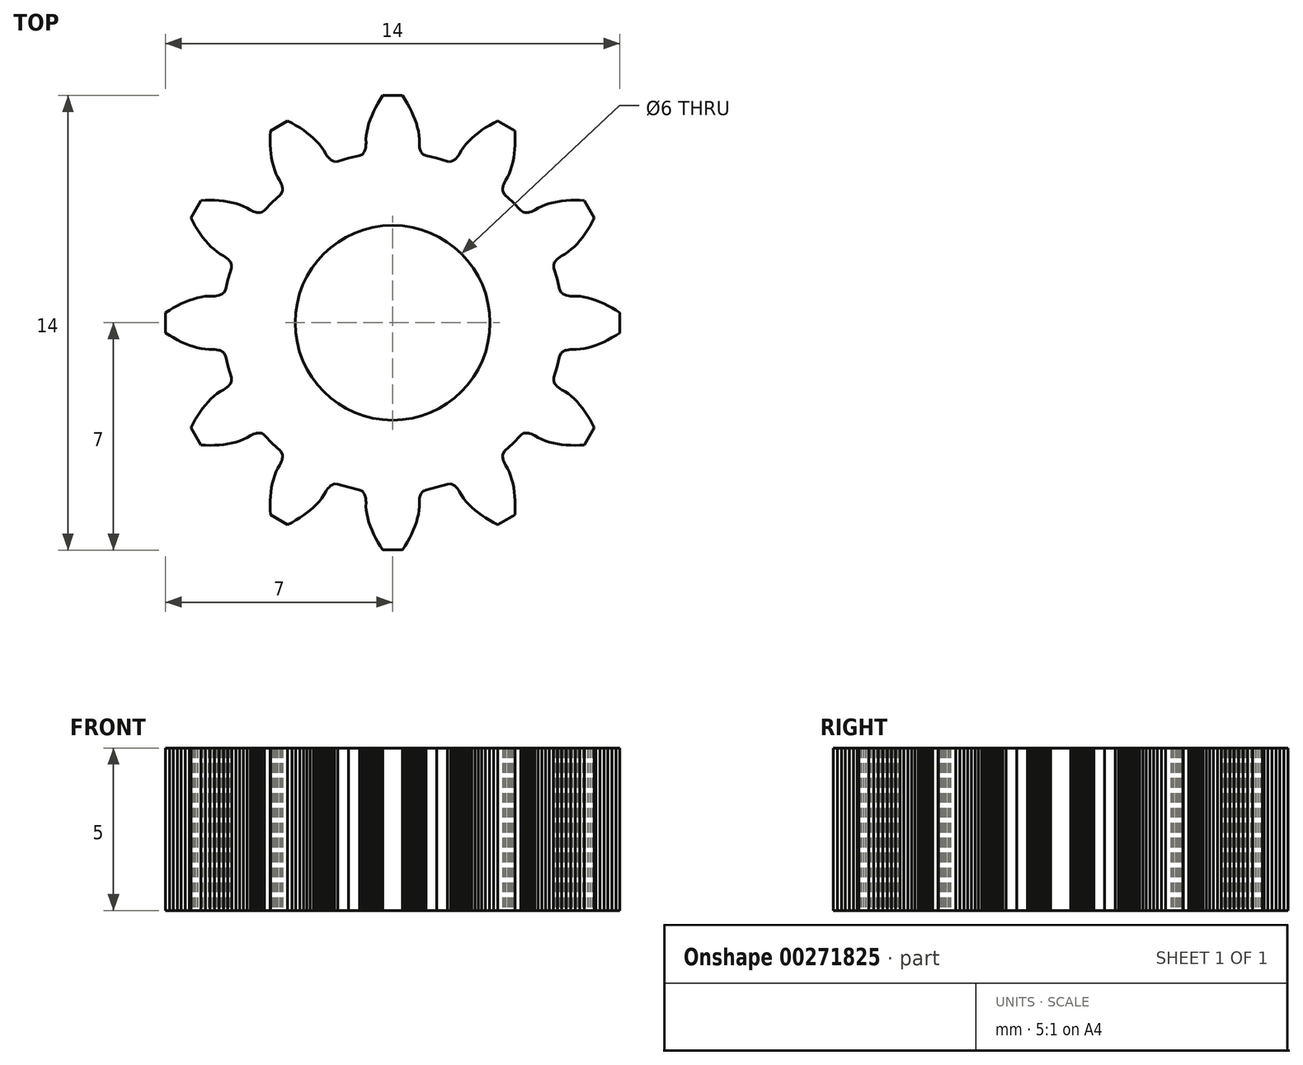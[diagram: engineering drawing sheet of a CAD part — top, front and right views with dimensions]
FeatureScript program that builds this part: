
annotation { "Feature Type Name" : "Feature", "Feature Type Description" : "" }
export const myFeature = defineFeature(function(context is Context, id is Id, definition is map)
    precondition{}
    {
        {
            var Q0;
            Q0=qCreatedBy(makeId("Top.planeOp"),FACE);
            var sketch = newSketch(context, id + "F0", { "sketchPlane" : qUnion([Q0])});
            skLineSegment(sketch, "E0", {"start": v(5.15, 1.02) * mm, "end": v(5.2, 0.93) * mm});
            skLineSegment(sketch, "E1", {"start": v(5.2, 0.93) * mm, "end": v(5.23, 0.9) * mm});
            skLineSegment(sketch, "E2", {"start": v(5.23, 0.9) * mm, "end": v(5.26, 0.88) * mm});
            skLineSegment(sketch, "E3", {"start": v(5.26, 0.88) * mm, "end": v(5.3, 0.86) * mm});
            skLineSegment(sketch, "E4", {"start": v(5.3, 0.86) * mm, "end": v(5.33, 0.85) * mm});
            skLineSegment(sketch, "E5", {"start": v(5.33, 0.85) * mm, "end": v(5.36, 0.84) * mm});
            skLineSegment(sketch, "E6", {"start": v(5.36, 0.84) * mm, "end": v(5.42, 0.83) * mm});
            skLineSegment(sketch, "E7", {"start": v(5.42, 0.83) * mm, "end": v(5.48, 0.82) * mm});
            skLineSegment(sketch, "E8", {"start": v(5.48, 0.82) * mm, "end": v(5.54, 0.82) * mm});
            skLineSegment(sketch, "E9", {"start": v(5.54, 0.82) * mm, "end": v(5.66, 0.82) * mm});
            skLineSegment(sketch, "E10", {"start": v(5.66, 0.82) * mm, "end": v(5.78, 0.81) * mm});
            skLineSegment(sketch, "E11", {"start": v(5.78, 0.81) * mm, "end": v(5.9, 0.8) * mm});
            skLineSegment(sketch, "E12", {"start": v(5.9, 0.8) * mm, "end": v(6.02, 0.77) * mm});
            skLineSegment(sketch, "E13", {"start": v(6.02, 0.77) * mm, "end": v(6.14, 0.73) * mm});
            skLineSegment(sketch, "E14", {"start": v(6.14, 0.73) * mm, "end": v(6.26, 0.69) * mm});
            skLineSegment(sketch, "E15", {"start": v(6.26, 0.69) * mm, "end": v(6.39, 0.64) * mm});
            skLineSegment(sketch, "E16", {"start": v(6.39, 0.64) * mm, "end": v(6.5, 0.59) * mm});
            skLineSegment(sketch, "E17", {"start": v(6.5, 0.59) * mm, "end": v(6.63, 0.52) * mm});
            skLineSegment(sketch, "E18", {"start": v(6.63, 0.52) * mm, "end": v(6.75, 0.46) * mm});
            skLineSegment(sketch, "E19", {"start": v(6.75, 0.46) * mm, "end": v(6.88, 0.39) * mm});
            skLineSegment(sketch, "E20", {"start": v(6.88, 0.39) * mm, "end": v(7, 0.3) * mm});
            skLineSegment(sketch, "E21", {"start": v(7, 0.3) * mm, "end": v(7, -0.3) * mm});
            skLineSegment(sketch, "E22", {"start": v(7, -0.3) * mm, "end": v(6.88, -0.39) * mm});
            skLineSegment(sketch, "E23", {"start": v(6.88, -0.39) * mm, "end": v(6.75, -0.46) * mm});
            skLineSegment(sketch, "E24", {"start": v(6.75, -0.46) * mm, "end": v(6.63, -0.52) * mm});
            skLineSegment(sketch, "E25", {"start": v(6.63, -0.52) * mm, "end": v(6.5, -0.59) * mm});
            skLineSegment(sketch, "E26", {"start": v(6.5, -0.59) * mm, "end": v(6.39, -0.64) * mm});
            skLineSegment(sketch, "E27", {"start": v(6.39, -0.64) * mm, "end": v(6.26, -0.69) * mm});
            skLineSegment(sketch, "E28", {"start": v(6.26, -0.69) * mm, "end": v(6.14, -0.73) * mm});
            skLineSegment(sketch, "E29", {"start": v(6.14, -0.73) * mm, "end": v(6.02, -0.77) * mm});
            skLineSegment(sketch, "E30", {"start": v(6.02, -0.77) * mm, "end": v(5.9, -0.8) * mm});
            skLineSegment(sketch, "E31", {"start": v(5.9, -0.8) * mm, "end": v(5.78, -0.81) * mm});
            skLineSegment(sketch, "E32", {"start": v(5.78, -0.81) * mm, "end": v(5.66, -0.82) * mm});
            skLineSegment(sketch, "E33", {"start": v(5.66, -0.82) * mm, "end": v(5.54, -0.82) * mm});
            skLineSegment(sketch, "E34", {"start": v(5.54, -0.82) * mm, "end": v(5.48, -0.82) * mm});
            skLineSegment(sketch, "E35", {"start": v(5.48, -0.82) * mm, "end": v(5.42, -0.83) * mm});
            skLineSegment(sketch, "E36", {"start": v(5.42, -0.83) * mm, "end": v(5.36, -0.84) * mm});
            skLineSegment(sketch, "E37", {"start": v(5.36, -0.84) * mm, "end": v(5.33, -0.85) * mm});
            skLineSegment(sketch, "E38", {"start": v(5.33, -0.85) * mm, "end": v(5.3, -0.86) * mm});
            skLineSegment(sketch, "E39", {"start": v(5.3, -0.86) * mm, "end": v(5.26, -0.88) * mm});
            skLineSegment(sketch, "E40", {"start": v(5.26, -0.88) * mm, "end": v(5.23, -0.9) * mm});
            skLineSegment(sketch, "E41", {"start": v(5.23, -0.9) * mm, "end": v(5.2, -0.93) * mm});
            skLineSegment(sketch, "E42", {"start": v(5.2, -0.93) * mm, "end": v(5.15, -1.02) * mm});
            skLineSegment(sketch, "E43", {"start": v(5.15, -1.02) * mm, "end": v(5.07, -1.36) * mm});
            skLineSegment(sketch, "E44", {"start": v(5.07, -1.36) * mm, "end": v(4.97, -1.69) * mm});
            skLineSegment(sketch, "E45", {"start": v(4.97, -1.69) * mm, "end": v(4.96, -1.79) * mm});
            skLineSegment(sketch, "E46", {"start": v(4.96, -1.79) * mm, "end": v(4.98, -1.83) * mm});
            skLineSegment(sketch, "E47", {"start": v(4.98, -1.83) * mm, "end": v(5, -1.87) * mm});
            skLineSegment(sketch, "E48", {"start": v(5, -1.87) * mm, "end": v(5.02, -1.9) * mm});
            skLineSegment(sketch, "E49", {"start": v(5.02, -1.9) * mm, "end": v(5.04, -1.93) * mm});
            skLineSegment(sketch, "E50", {"start": v(5.04, -1.93) * mm, "end": v(5.06, -1.95) * mm});
            skLineSegment(sketch, "E51", {"start": v(5.06, -1.95) * mm, "end": v(5.1, -2) * mm});
            skLineSegment(sketch, "E52", {"start": v(5.1, -2) * mm, "end": v(5.15, -2.03) * mm});
            skLineSegment(sketch, "E53", {"start": v(5.15, -2.03) * mm, "end": v(5.2, -2.06) * mm});
            skLineSegment(sketch, "E54", {"start": v(5.2, -2.06) * mm, "end": v(5.3, -2.12) * mm});
            skLineSegment(sketch, "E55", {"start": v(5.3, -2.12) * mm, "end": v(5.4, -2.18) * mm});
            skLineSegment(sketch, "E56", {"start": v(5.4, -2.18) * mm, "end": v(5.5, -2.26) * mm});
            skLineSegment(sketch, "E57", {"start": v(5.5, -2.26) * mm, "end": v(5.6, -2.35) * mm});
            skLineSegment(sketch, "E58", {"start": v(5.6, -2.35) * mm, "end": v(5.68, -2.44) * mm});
            skLineSegment(sketch, "E59", {"start": v(5.68, -2.44) * mm, "end": v(5.77, -2.53) * mm});
            skLineSegment(sketch, "E60", {"start": v(5.77, -2.53) * mm, "end": v(5.85, -2.64) * mm});
            skLineSegment(sketch, "E61", {"start": v(5.85, -2.64) * mm, "end": v(5.93, -2.75) * mm});
            skLineSegment(sketch, "E62", {"start": v(5.93, -2.75) * mm, "end": v(6, -2.86) * mm});
            skLineSegment(sketch, "E63", {"start": v(6, -2.86) * mm, "end": v(6.08, -2.98) * mm});
            skLineSegment(sketch, "E64", {"start": v(6.08, -2.98) * mm, "end": v(6.15, -3.1) * mm});
            skLineSegment(sketch, "E65", {"start": v(6.15, -3.1) * mm, "end": v(6.21, -3.23) * mm});
            skLineSegment(sketch, "E66", {"start": v(6.21, -3.23) * mm, "end": v(5.9, -3.76) * mm});
            skLineSegment(sketch, "E67", {"start": v(5.9, -3.76) * mm, "end": v(5.76, -3.77) * mm});
            skLineSegment(sketch, "E68", {"start": v(5.76, -3.77) * mm, "end": v(5.62, -3.77) * mm});
            skLineSegment(sketch, "E69", {"start": v(5.62, -3.77) * mm, "end": v(5.48, -3.77) * mm});
            skLineSegment(sketch, "E70", {"start": v(5.48, -3.77) * mm, "end": v(5.34, -3.76) * mm});
            skLineSegment(sketch, "E71", {"start": v(5.34, -3.76) * mm, "end": v(5.21, -3.75) * mm});
            skLineSegment(sketch, "E72", {"start": v(5.21, -3.75) * mm, "end": v(5.08, -3.73) * mm});
            skLineSegment(sketch, "E73", {"start": v(5.08, -3.73) * mm, "end": v(4.95, -3.7) * mm});
            skLineSegment(sketch, "E74", {"start": v(4.95, -3.7) * mm, "end": v(4.83, -3.67) * mm});
            skLineSegment(sketch, "E75", {"start": v(4.83, -3.67) * mm, "end": v(4.7, -3.64) * mm});
            skLineSegment(sketch, "E76", {"start": v(4.7, -3.64) * mm, "end": v(4.6, -3.6) * mm});
            skLineSegment(sketch, "E77", {"start": v(4.6, -3.6) * mm, "end": v(4.49, -3.54) * mm});
            skLineSegment(sketch, "E78", {"start": v(4.49, -3.54) * mm, "end": v(4.39, -3.48) * mm});
            skLineSegment(sketch, "E79", {"start": v(4.39, -3.48) * mm, "end": v(4.33, -3.45) * mm});
            skLineSegment(sketch, "E80", {"start": v(4.33, -3.45) * mm, "end": v(4.28, -3.43) * mm});
            skLineSegment(sketch, "E81", {"start": v(4.28, -3.43) * mm, "end": v(4.22, -3.4) * mm});
            skLineSegment(sketch, "E82", {"start": v(4.22, -3.4) * mm, "end": v(4.19, -3.4) * mm});
            skLineSegment(sketch, "E83", {"start": v(4.19, -3.4) * mm, "end": v(4.15, -3.4) * mm});
            skLineSegment(sketch, "E84", {"start": v(4.15, -3.4) * mm, "end": v(4.12, -3.4) * mm});
            skLineSegment(sketch, "E85", {"start": v(4.12, -3.4) * mm, "end": v(4.08, -3.4) * mm});
            skLineSegment(sketch, "E86", {"start": v(4.08, -3.4) * mm, "end": v(4.03, -3.4) * mm});
            skLineSegment(sketch, "E87", {"start": v(4.03, -3.4) * mm, "end": v(3.94, -3.46) * mm});
            skLineSegment(sketch, "E88", {"start": v(3.94, -3.46) * mm, "end": v(3.7, -3.7) * mm});
            skLineSegment(sketch, "E89", {"start": v(3.7, -3.7) * mm, "end": v(3.46, -3.94) * mm});
            skLineSegment(sketch, "E90", {"start": v(3.46, -3.94) * mm, "end": v(3.4, -4.03) * mm});
            skLineSegment(sketch, "E91", {"start": v(3.4, -4.03) * mm, "end": v(3.4, -4.08) * mm});
            skLineSegment(sketch, "E92", {"start": v(3.4, -4.08) * mm, "end": v(3.4, -4.12) * mm});
            skLineSegment(sketch, "E93", {"start": v(3.4, -4.12) * mm, "end": v(3.4, -4.15) * mm});
            skLineSegment(sketch, "E94", {"start": v(3.4, -4.15) * mm, "end": v(3.4, -4.19) * mm});
            skLineSegment(sketch, "E95", {"start": v(3.4, -4.19) * mm, "end": v(3.4, -4.22) * mm});
            skLineSegment(sketch, "E96", {"start": v(3.4, -4.22) * mm, "end": v(3.43, -4.28) * mm});
            skLineSegment(sketch, "E97", {"start": v(3.43, -4.28) * mm, "end": v(3.45, -4.33) * mm});
            skLineSegment(sketch, "E98", {"start": v(3.45, -4.33) * mm, "end": v(3.48, -4.39) * mm});
            skLineSegment(sketch, "E99", {"start": v(3.48, -4.39) * mm, "end": v(3.54, -4.49) * mm});
            skLineSegment(sketch, "E100", {"start": v(3.54, -4.49) * mm, "end": v(3.6, -4.6) * mm});
            skLineSegment(sketch, "E101", {"start": v(3.6, -4.6) * mm, "end": v(3.64, -4.7) * mm});
            skLineSegment(sketch, "E102", {"start": v(3.64, -4.7) * mm, "end": v(3.67, -4.83) * mm});
            skLineSegment(sketch, "E103", {"start": v(3.67, -4.83) * mm, "end": v(3.7, -4.95) * mm});
            skLineSegment(sketch, "E104", {"start": v(3.7, -4.95) * mm, "end": v(3.73, -5.08) * mm});
            skLineSegment(sketch, "E105", {"start": v(3.73, -5.08) * mm, "end": v(3.75, -5.21) * mm});
            skLineSegment(sketch, "E106", {"start": v(3.75, -5.21) * mm, "end": v(3.76, -5.34) * mm});
            skLineSegment(sketch, "E107", {"start": v(3.76, -5.34) * mm, "end": v(3.77, -5.48) * mm});
            skLineSegment(sketch, "E108", {"start": v(3.77, -5.48) * mm, "end": v(3.77, -5.62) * mm});
            skLineSegment(sketch, "E109", {"start": v(3.77, -5.62) * mm, "end": v(3.77, -5.76) * mm});
            skLineSegment(sketch, "E110", {"start": v(3.77, -5.76) * mm, "end": v(3.76, -5.9) * mm});
            skLineSegment(sketch, "E111", {"start": v(3.76, -5.9) * mm, "end": v(3.23, -6.21) * mm});
            skLineSegment(sketch, "E112", {"start": v(3.23, -6.21) * mm, "end": v(3.1, -6.15) * mm});
            skLineSegment(sketch, "E113", {"start": v(3.1, -6.15) * mm, "end": v(2.98, -6.08) * mm});
            skLineSegment(sketch, "E114", {"start": v(2.98, -6.08) * mm, "end": v(2.86, -6) * mm});
            skLineSegment(sketch, "E115", {"start": v(2.86, -6) * mm, "end": v(2.75, -5.93) * mm});
            skLineSegment(sketch, "E116", {"start": v(2.75, -5.93) * mm, "end": v(2.64, -5.85) * mm});
            skLineSegment(sketch, "E117", {"start": v(2.64, -5.85) * mm, "end": v(2.53, -5.77) * mm});
            skLineSegment(sketch, "E118", {"start": v(2.53, -5.77) * mm, "end": v(2.44, -5.68) * mm});
            skLineSegment(sketch, "E119", {"start": v(2.44, -5.68) * mm, "end": v(2.35, -5.6) * mm});
            skLineSegment(sketch, "E120", {"start": v(2.35, -5.6) * mm, "end": v(2.26, -5.5) * mm});
            skLineSegment(sketch, "E121", {"start": v(2.26, -5.5) * mm, "end": v(2.18, -5.4) * mm});
            skLineSegment(sketch, "E122", {"start": v(2.18, -5.4) * mm, "end": v(2.12, -5.3) * mm});
            skLineSegment(sketch, "E123", {"start": v(2.12, -5.3) * mm, "end": v(2.06, -5.2) * mm});
            skLineSegment(sketch, "E124", {"start": v(2.06, -5.2) * mm, "end": v(2.03, -5.15) * mm});
            skLineSegment(sketch, "E125", {"start": v(2.03, -5.15) * mm, "end": v(2, -5.1) * mm});
            skLineSegment(sketch, "E126", {"start": v(2, -5.1) * mm, "end": v(1.95, -5.06) * mm});
            skLineSegment(sketch, "E127", {"start": v(1.95, -5.06) * mm, "end": v(1.93, -5.04) * mm});
            skLineSegment(sketch, "E128", {"start": v(1.93, -5.04) * mm, "end": v(1.9, -5.02) * mm});
            skLineSegment(sketch, "E129", {"start": v(1.9, -5.02) * mm, "end": v(1.87, -5) * mm});
            skLineSegment(sketch, "E130", {"start": v(1.87, -5) * mm, "end": v(1.83, -4.98) * mm});
            skLineSegment(sketch, "E131", {"start": v(1.83, -4.98) * mm, "end": v(1.79, -4.96) * mm});
            skLineSegment(sketch, "E132", {"start": v(1.79, -4.96) * mm, "end": v(1.69, -4.97) * mm});
            skLineSegment(sketch, "E133", {"start": v(1.69, -4.97) * mm, "end": v(1.36, -5.07) * mm});
            skLineSegment(sketch, "E134", {"start": v(1.36, -5.07) * mm, "end": v(1.02, -5.15) * mm});
            skLineSegment(sketch, "E135", {"start": v(1.02, -5.15) * mm, "end": v(0.93, -5.2) * mm});
            skLineSegment(sketch, "E136", {"start": v(0.93, -5.2) * mm, "end": v(0.9, -5.23) * mm});
            skLineSegment(sketch, "E137", {"start": v(0.9, -5.23) * mm, "end": v(0.88, -5.26) * mm});
            skLineSegment(sketch, "E138", {"start": v(0.88, -5.26) * mm, "end": v(0.86, -5.3) * mm});
            skLineSegment(sketch, "E139", {"start": v(0.86, -5.3) * mm, "end": v(0.85, -5.33) * mm});
            skLineSegment(sketch, "E140", {"start": v(0.85, -5.33) * mm, "end": v(0.84, -5.36) * mm});
            skLineSegment(sketch, "E141", {"start": v(0.84, -5.36) * mm, "end": v(0.83, -5.42) * mm});
            skLineSegment(sketch, "E142", {"start": v(0.83, -5.42) * mm, "end": v(0.82, -5.48) * mm});
            skLineSegment(sketch, "E143", {"start": v(0.82, -5.48) * mm, "end": v(0.82, -5.54) * mm});
            skLineSegment(sketch, "E144", {"start": v(0.82, -5.54) * mm, "end": v(0.82, -5.66) * mm});
            skLineSegment(sketch, "E145", {"start": v(0.82, -5.66) * mm, "end": v(0.81, -5.78) * mm});
            skLineSegment(sketch, "E146", {"start": v(0.81, -5.78) * mm, "end": v(0.8, -5.9) * mm});
            skLineSegment(sketch, "E147", {"start": v(0.8, -5.9) * mm, "end": v(0.77, -6.02) * mm});
            skLineSegment(sketch, "E148", {"start": v(0.77, -6.02) * mm, "end": v(0.73, -6.14) * mm});
            skLineSegment(sketch, "E149", {"start": v(0.73, -6.14) * mm, "end": v(0.69, -6.26) * mm});
            skLineSegment(sketch, "E150", {"start": v(0.69, -6.26) * mm, "end": v(0.64, -6.39) * mm});
            skLineSegment(sketch, "E151", {"start": v(0.64, -6.39) * mm, "end": v(0.59, -6.5) * mm});
            skLineSegment(sketch, "E152", {"start": v(0.59, -6.5) * mm, "end": v(0.52, -6.63) * mm});
            skLineSegment(sketch, "E153", {"start": v(0.52, -6.63) * mm, "end": v(0.46, -6.75) * mm});
            skLineSegment(sketch, "E154", {"start": v(0.46, -6.75) * mm, "end": v(0.39, -6.88) * mm});
            skLineSegment(sketch, "E155", {"start": v(0.39, -6.88) * mm, "end": v(0.3, -7) * mm});
            skLineSegment(sketch, "E156", {"start": v(0.3, -7) * mm, "end": v(-0.3, -7) * mm});
            skLineSegment(sketch, "E157", {"start": v(-0.3, -7) * mm, "end": v(-0.39, -6.88) * mm});
            skLineSegment(sketch, "E158", {"start": v(-0.39, -6.88) * mm, "end": v(-0.46, -6.75) * mm});
            skLineSegment(sketch, "E159", {"start": v(-0.46, -6.75) * mm, "end": v(-0.52, -6.63) * mm});
            skLineSegment(sketch, "E160", {"start": v(-0.52, -6.63) * mm, "end": v(-0.59, -6.5) * mm});
            skLineSegment(sketch, "E161", {"start": v(-0.59, -6.5) * mm, "end": v(-0.64, -6.39) * mm});
            skLineSegment(sketch, "E162", {"start": v(-0.64, -6.39) * mm, "end": v(-0.69, -6.26) * mm});
            skLineSegment(sketch, "E163", {"start": v(-0.69, -6.26) * mm, "end": v(-0.73, -6.14) * mm});
            skLineSegment(sketch, "E164", {"start": v(-0.73, -6.14) * mm, "end": v(-0.77, -6.02) * mm});
            skLineSegment(sketch, "E165", {"start": v(-0.77, -6.02) * mm, "end": v(-0.8, -5.9) * mm});
            skLineSegment(sketch, "E166", {"start": v(-0.8, -5.9) * mm, "end": v(-0.81, -5.78) * mm});
            skLineSegment(sketch, "E167", {"start": v(-0.81, -5.78) * mm, "end": v(-0.82, -5.66) * mm});
            skLineSegment(sketch, "E168", {"start": v(-0.82, -5.66) * mm, "end": v(-0.82, -5.54) * mm});
            skLineSegment(sketch, "E169", {"start": v(-0.82, -5.54) * mm, "end": v(-0.82, -5.48) * mm});
            skLineSegment(sketch, "E170", {"start": v(-0.82, -5.48) * mm, "end": v(-0.83, -5.42) * mm});
            skLineSegment(sketch, "E171", {"start": v(-0.83, -5.42) * mm, "end": v(-0.84, -5.36) * mm});
            skLineSegment(sketch, "E172", {"start": v(-0.84, -5.36) * mm, "end": v(-0.85, -5.33) * mm});
            skLineSegment(sketch, "E173", {"start": v(-0.85, -5.33) * mm, "end": v(-0.86, -5.3) * mm});
            skLineSegment(sketch, "E174", {"start": v(-0.86, -5.3) * mm, "end": v(-0.88, -5.26) * mm});
            skLineSegment(sketch, "E175", {"start": v(-0.88, -5.26) * mm, "end": v(-0.9, -5.23) * mm});
            skLineSegment(sketch, "E176", {"start": v(-0.9, -5.23) * mm, "end": v(-0.93, -5.2) * mm});
            skLineSegment(sketch, "E177", {"start": v(-0.93, -5.2) * mm, "end": v(-1.02, -5.15) * mm});
            skLineSegment(sketch, "E178", {"start": v(-1.02, -5.15) * mm, "end": v(-1.36, -5.07) * mm});
            skLineSegment(sketch, "E179", {"start": v(-1.36, -5.07) * mm, "end": v(-1.69, -4.97) * mm});
            skLineSegment(sketch, "E180", {"start": v(-1.69, -4.97) * mm, "end": v(-1.79, -4.96) * mm});
            skLineSegment(sketch, "E181", {"start": v(-1.79, -4.96) * mm, "end": v(-1.83, -4.98) * mm});
            skLineSegment(sketch, "E182", {"start": v(-1.83, -4.98) * mm, "end": v(-1.87, -5) * mm});
            skLineSegment(sketch, "E183", {"start": v(-1.87, -5) * mm, "end": v(-1.9, -5.02) * mm});
            skLineSegment(sketch, "E184", {"start": v(-1.9, -5.02) * mm, "end": v(-1.93, -5.04) * mm});
            skLineSegment(sketch, "E185", {"start": v(-1.93, -5.04) * mm, "end": v(-1.95, -5.06) * mm});
            skLineSegment(sketch, "E186", {"start": v(-1.95, -5.06) * mm, "end": v(-2, -5.1) * mm});
            skLineSegment(sketch, "E187", {"start": v(-2, -5.1) * mm, "end": v(-2.03, -5.15) * mm});
            skLineSegment(sketch, "E188", {"start": v(-2.03, -5.15) * mm, "end": v(-2.06, -5.2) * mm});
            skLineSegment(sketch, "E189", {"start": v(-2.06, -5.2) * mm, "end": v(-2.12, -5.3) * mm});
            skLineSegment(sketch, "E190", {"start": v(-2.12, -5.3) * mm, "end": v(-2.18, -5.4) * mm});
            skLineSegment(sketch, "E191", {"start": v(-2.18, -5.4) * mm, "end": v(-2.26, -5.5) * mm});
            skLineSegment(sketch, "E192", {"start": v(-2.26, -5.5) * mm, "end": v(-2.35, -5.6) * mm});
            skLineSegment(sketch, "E193", {"start": v(-2.35, -5.6) * mm, "end": v(-2.44, -5.68) * mm});
            skLineSegment(sketch, "E194", {"start": v(-2.44, -5.68) * mm, "end": v(-2.53, -5.77) * mm});
            skLineSegment(sketch, "E195", {"start": v(-2.53, -5.77) * mm, "end": v(-2.64, -5.85) * mm});
            skLineSegment(sketch, "E196", {"start": v(-2.64, -5.85) * mm, "end": v(-2.75, -5.93) * mm});
            skLineSegment(sketch, "E197", {"start": v(-2.75, -5.93) * mm, "end": v(-2.86, -6) * mm});
            skLineSegment(sketch, "E198", {"start": v(-2.86, -6) * mm, "end": v(-2.98, -6.08) * mm});
            skLineSegment(sketch, "E199", {"start": v(-2.98, -6.08) * mm, "end": v(-3.1, -6.15) * mm});
            skLineSegment(sketch, "E200", {"start": v(-3.1, -6.15) * mm, "end": v(-3.23, -6.21) * mm});
            skLineSegment(sketch, "E201", {"start": v(-3.23, -6.21) * mm, "end": v(-3.76, -5.9) * mm});
            skLineSegment(sketch, "E202", {"start": v(-3.76, -5.9) * mm, "end": v(-3.77, -5.76) * mm});
            skLineSegment(sketch, "E203", {"start": v(-3.77, -5.76) * mm, "end": v(-3.77, -5.62) * mm});
            skLineSegment(sketch, "E204", {"start": v(-3.77, -5.62) * mm, "end": v(-3.77, -5.48) * mm});
            skLineSegment(sketch, "E205", {"start": v(-3.77, -5.48) * mm, "end": v(-3.76, -5.34) * mm});
            skLineSegment(sketch, "E206", {"start": v(-3.76, -5.34) * mm, "end": v(-3.75, -5.21) * mm});
            skLineSegment(sketch, "E207", {"start": v(-3.75, -5.21) * mm, "end": v(-3.73, -5.08) * mm});
            skLineSegment(sketch, "E208", {"start": v(-3.73, -5.08) * mm, "end": v(-3.7, -4.95) * mm});
            skLineSegment(sketch, "E209", {"start": v(-3.7, -4.95) * mm, "end": v(-3.67, -4.83) * mm});
            skLineSegment(sketch, "E210", {"start": v(-3.67, -4.83) * mm, "end": v(-3.64, -4.7) * mm});
            skLineSegment(sketch, "E211", {"start": v(-3.64, -4.7) * mm, "end": v(-3.6, -4.6) * mm});
            skLineSegment(sketch, "E212", {"start": v(-3.6, -4.6) * mm, "end": v(-3.54, -4.49) * mm});
            skLineSegment(sketch, "E213", {"start": v(-3.54, -4.49) * mm, "end": v(-3.48, -4.39) * mm});
            skLineSegment(sketch, "E214", {"start": v(-3.48, -4.39) * mm, "end": v(-3.45, -4.33) * mm});
            skLineSegment(sketch, "E215", {"start": v(-3.45, -4.33) * mm, "end": v(-3.43, -4.28) * mm});
            skLineSegment(sketch, "E216", {"start": v(-3.43, -4.28) * mm, "end": v(-3.4, -4.22) * mm});
            skLineSegment(sketch, "E217", {"start": v(-3.4, -4.22) * mm, "end": v(-3.4, -4.19) * mm});
            skLineSegment(sketch, "E218", {"start": v(-3.4, -4.19) * mm, "end": v(-3.4, -4.15) * mm});
            skLineSegment(sketch, "E219", {"start": v(-3.4, -4.15) * mm, "end": v(-3.4, -4.12) * mm});
            skLineSegment(sketch, "E220", {"start": v(-3.4, -4.12) * mm, "end": v(-3.4, -4.08) * mm});
            skLineSegment(sketch, "E221", {"start": v(-3.4, -4.08) * mm, "end": v(-3.4, -4.03) * mm});
            skLineSegment(sketch, "E222", {"start": v(-3.4, -4.03) * mm, "end": v(-3.46, -3.94) * mm});
            skLineSegment(sketch, "E223", {"start": v(-3.46, -3.94) * mm, "end": v(-3.7, -3.7) * mm});
            skLineSegment(sketch, "E224", {"start": v(-3.7, -3.7) * mm, "end": v(-3.94, -3.46) * mm});
            skLineSegment(sketch, "E225", {"start": v(-3.94, -3.46) * mm, "end": v(-4.03, -3.4) * mm});
            skLineSegment(sketch, "E226", {"start": v(-4.03, -3.4) * mm, "end": v(-4.08, -3.4) * mm});
            skLineSegment(sketch, "E227", {"start": v(-4.08, -3.4) * mm, "end": v(-4.12, -3.4) * mm});
            skLineSegment(sketch, "E228", {"start": v(-4.12, -3.4) * mm, "end": v(-4.15, -3.4) * mm});
            skLineSegment(sketch, "E229", {"start": v(-4.15, -3.4) * mm, "end": v(-4.19, -3.4) * mm});
            skLineSegment(sketch, "E230", {"start": v(-4.19, -3.4) * mm, "end": v(-4.22, -3.4) * mm});
            skLineSegment(sketch, "E231", {"start": v(-4.22, -3.4) * mm, "end": v(-4.28, -3.43) * mm});
            skLineSegment(sketch, "E232", {"start": v(-4.28, -3.43) * mm, "end": v(-4.33, -3.45) * mm});
            skLineSegment(sketch, "E233", {"start": v(-4.33, -3.45) * mm, "end": v(-4.39, -3.48) * mm});
            skLineSegment(sketch, "E234", {"start": v(-4.39, -3.48) * mm, "end": v(-4.49, -3.54) * mm});
            skLineSegment(sketch, "E235", {"start": v(-4.49, -3.54) * mm, "end": v(-4.6, -3.6) * mm});
            skLineSegment(sketch, "E236", {"start": v(-4.6, -3.6) * mm, "end": v(-4.7, -3.64) * mm});
            skLineSegment(sketch, "E237", {"start": v(-4.7, -3.64) * mm, "end": v(-4.83, -3.67) * mm});
            skLineSegment(sketch, "E238", {"start": v(-4.83, -3.67) * mm, "end": v(-4.95, -3.7) * mm});
            skLineSegment(sketch, "E239", {"start": v(-4.95, -3.7) * mm, "end": v(-5.08, -3.73) * mm});
            skLineSegment(sketch, "E240", {"start": v(-5.08, -3.73) * mm, "end": v(-5.21, -3.75) * mm});
            skLineSegment(sketch, "E241", {"start": v(-5.21, -3.75) * mm, "end": v(-5.34, -3.76) * mm});
            skLineSegment(sketch, "E242", {"start": v(-5.34, -3.76) * mm, "end": v(-5.48, -3.77) * mm});
            skLineSegment(sketch, "E243", {"start": v(-5.48, -3.77) * mm, "end": v(-5.62, -3.77) * mm});
            skLineSegment(sketch, "E244", {"start": v(-5.62, -3.77) * mm, "end": v(-5.76, -3.77) * mm});
            skLineSegment(sketch, "E245", {"start": v(-5.76, -3.77) * mm, "end": v(-5.9, -3.76) * mm});
            skLineSegment(sketch, "E246", {"start": v(-5.9, -3.76) * mm, "end": v(-6.21, -3.23) * mm});
            skLineSegment(sketch, "E247", {"start": v(-6.21, -3.23) * mm, "end": v(-6.15, -3.1) * mm});
            skLineSegment(sketch, "E248", {"start": v(-6.15, -3.1) * mm, "end": v(-6.08, -2.98) * mm});
            skLineSegment(sketch, "E249", {"start": v(-6.08, -2.98) * mm, "end": v(-6, -2.86) * mm});
            skLineSegment(sketch, "E250", {"start": v(-6, -2.86) * mm, "end": v(-5.93, -2.75) * mm});
            skLineSegment(sketch, "E251", {"start": v(-5.93, -2.75) * mm, "end": v(-5.85, -2.64) * mm});
            skLineSegment(sketch, "E252", {"start": v(-5.85, -2.64) * mm, "end": v(-5.77, -2.53) * mm});
            skLineSegment(sketch, "E253", {"start": v(-5.77, -2.53) * mm, "end": v(-5.68, -2.44) * mm});
            skLineSegment(sketch, "E254", {"start": v(-5.68, -2.44) * mm, "end": v(-5.6, -2.35) * mm});
            skLineSegment(sketch, "E255", {"start": v(-5.6, -2.35) * mm, "end": v(-5.5, -2.26) * mm});
            skLineSegment(sketch, "E256", {"start": v(-5.5, -2.26) * mm, "end": v(-5.4, -2.18) * mm});
            skLineSegment(sketch, "E257", {"start": v(-5.4, -2.18) * mm, "end": v(-5.3, -2.12) * mm});
            skLineSegment(sketch, "E258", {"start": v(-5.3, -2.12) * mm, "end": v(-5.2, -2.06) * mm});
            skLineSegment(sketch, "E259", {"start": v(-5.2, -2.06) * mm, "end": v(-5.15, -2.03) * mm});
            skLineSegment(sketch, "E260", {"start": v(-5.15, -2.03) * mm, "end": v(-5.1, -2) * mm});
            skLineSegment(sketch, "E261", {"start": v(-5.1, -2) * mm, "end": v(-5.06, -1.95) * mm});
            skLineSegment(sketch, "E262", {"start": v(-5.06, -1.95) * mm, "end": v(-5.04, -1.93) * mm});
            skLineSegment(sketch, "E263", {"start": v(-5.04, -1.93) * mm, "end": v(-5.02, -1.9) * mm});
            skLineSegment(sketch, "E264", {"start": v(-5.02, -1.9) * mm, "end": v(-5, -1.87) * mm});
            skLineSegment(sketch, "E265", {"start": v(-5, -1.87) * mm, "end": v(-4.98, -1.83) * mm});
            skLineSegment(sketch, "E266", {"start": v(-4.98, -1.83) * mm, "end": v(-4.96, -1.79) * mm});
            skLineSegment(sketch, "E267", {"start": v(-4.96, -1.79) * mm, "end": v(-4.97, -1.69) * mm});
            skLineSegment(sketch, "E268", {"start": v(-4.97, -1.69) * mm, "end": v(-5.07, -1.36) * mm});
            skLineSegment(sketch, "E269", {"start": v(-5.07, -1.36) * mm, "end": v(-5.15, -1.02) * mm});
            skLineSegment(sketch, "E270", {"start": v(-5.15, -1.02) * mm, "end": v(-5.2, -0.93) * mm});
            skLineSegment(sketch, "E271", {"start": v(-5.2, -0.93) * mm, "end": v(-5.23, -0.9) * mm});
            skLineSegment(sketch, "E272", {"start": v(-5.23, -0.9) * mm, "end": v(-5.26, -0.88) * mm});
            skLineSegment(sketch, "E273", {"start": v(-5.26, -0.88) * mm, "end": v(-5.3, -0.86) * mm});
            skLineSegment(sketch, "E274", {"start": v(-5.3, -0.86) * mm, "end": v(-5.33, -0.85) * mm});
            skLineSegment(sketch, "E275", {"start": v(-5.33, -0.85) * mm, "end": v(-5.36, -0.84) * mm});
            skLineSegment(sketch, "E276", {"start": v(-5.36, -0.84) * mm, "end": v(-5.42, -0.83) * mm});
            skLineSegment(sketch, "E277", {"start": v(-5.42, -0.83) * mm, "end": v(-5.48, -0.82) * mm});
            skLineSegment(sketch, "E278", {"start": v(-5.48, -0.82) * mm, "end": v(-5.54, -0.82) * mm});
            skLineSegment(sketch, "E279", {"start": v(-5.54, -0.82) * mm, "end": v(-5.66, -0.82) * mm});
            skLineSegment(sketch, "E280", {"start": v(-5.66, -0.82) * mm, "end": v(-5.78, -0.81) * mm});
            skLineSegment(sketch, "E281", {"start": v(-5.78, -0.81) * mm, "end": v(-5.9, -0.8) * mm});
            skLineSegment(sketch, "E282", {"start": v(-5.9, -0.8) * mm, "end": v(-6.02, -0.77) * mm});
            skLineSegment(sketch, "E283", {"start": v(-6.02, -0.77) * mm, "end": v(-6.14, -0.73) * mm});
            skLineSegment(sketch, "E284", {"start": v(-6.14, -0.73) * mm, "end": v(-6.26, -0.69) * mm});
            skLineSegment(sketch, "E285", {"start": v(-6.26, -0.69) * mm, "end": v(-6.39, -0.64) * mm});
            skLineSegment(sketch, "E286", {"start": v(-6.39, -0.64) * mm, "end": v(-6.5, -0.59) * mm});
            skLineSegment(sketch, "E287", {"start": v(-6.5, -0.59) * mm, "end": v(-6.63, -0.52) * mm});
            skLineSegment(sketch, "E288", {"start": v(-6.63, -0.52) * mm, "end": v(-6.75, -0.46) * mm});
            skLineSegment(sketch, "E289", {"start": v(-6.75, -0.46) * mm, "end": v(-6.88, -0.39) * mm});
            skLineSegment(sketch, "E290", {"start": v(-6.88, -0.39) * mm, "end": v(-7, -0.3) * mm});
            skLineSegment(sketch, "E291", {"start": v(-7, -0.3) * mm, "end": v(-7, 0.3) * mm});
            skLineSegment(sketch, "E292", {"start": v(-7, 0.3) * mm, "end": v(-6.88, 0.39) * mm});
            skLineSegment(sketch, "E293", {"start": v(-6.88, 0.39) * mm, "end": v(-6.75, 0.46) * mm});
            skLineSegment(sketch, "E294", {"start": v(-6.75, 0.46) * mm, "end": v(-6.63, 0.52) * mm});
            skLineSegment(sketch, "E295", {"start": v(-6.63, 0.52) * mm, "end": v(-6.5, 0.59) * mm});
            skLineSegment(sketch, "E296", {"start": v(-6.5, 0.59) * mm, "end": v(-6.39, 0.64) * mm});
            skLineSegment(sketch, "E297", {"start": v(-6.39, 0.64) * mm, "end": v(-6.26, 0.69) * mm});
            skLineSegment(sketch, "E298", {"start": v(-6.26, 0.69) * mm, "end": v(-6.14, 0.73) * mm});
            skLineSegment(sketch, "E299", {"start": v(-6.14, 0.73) * mm, "end": v(-6.02, 0.77) * mm});
            skLineSegment(sketch, "E300", {"start": v(-6.02, 0.77) * mm, "end": v(-5.9, 0.8) * mm});
            skLineSegment(sketch, "E301", {"start": v(-5.9, 0.8) * mm, "end": v(-5.78, 0.81) * mm});
            skLineSegment(sketch, "E302", {"start": v(-5.78, 0.81) * mm, "end": v(-5.66, 0.82) * mm});
            skLineSegment(sketch, "E303", {"start": v(-5.66, 0.82) * mm, "end": v(-5.54, 0.82) * mm});
            skLineSegment(sketch, "E304", {"start": v(-5.54, 0.82) * mm, "end": v(-5.48, 0.82) * mm});
            skLineSegment(sketch, "E305", {"start": v(-5.48, 0.82) * mm, "end": v(-5.42, 0.83) * mm});
            skLineSegment(sketch, "E306", {"start": v(-5.42, 0.83) * mm, "end": v(-5.36, 0.84) * mm});
            skLineSegment(sketch, "E307", {"start": v(-5.36, 0.84) * mm, "end": v(-5.33, 0.85) * mm});
            skLineSegment(sketch, "E308", {"start": v(-5.33, 0.85) * mm, "end": v(-5.3, 0.86) * mm});
            skLineSegment(sketch, "E309", {"start": v(-5.3, 0.86) * mm, "end": v(-5.26, 0.88) * mm});
            skLineSegment(sketch, "E310", {"start": v(-5.26, 0.88) * mm, "end": v(-5.23, 0.9) * mm});
            skLineSegment(sketch, "E311", {"start": v(-5.23, 0.9) * mm, "end": v(-5.2, 0.93) * mm});
            skLineSegment(sketch, "E312", {"start": v(-5.2, 0.93) * mm, "end": v(-5.15, 1.02) * mm});
            skLineSegment(sketch, "E313", {"start": v(-5.15, 1.02) * mm, "end": v(-5.07, 1.36) * mm});
            skLineSegment(sketch, "E314", {"start": v(-5.07, 1.36) * mm, "end": v(-4.97, 1.69) * mm});
            skLineSegment(sketch, "E315", {"start": v(-4.97, 1.69) * mm, "end": v(-4.96, 1.79) * mm});
            skLineSegment(sketch, "E316", {"start": v(-4.96, 1.79) * mm, "end": v(-4.98, 1.83) * mm});
            skLineSegment(sketch, "E317", {"start": v(-4.98, 1.83) * mm, "end": v(-5, 1.87) * mm});
            skLineSegment(sketch, "E318", {"start": v(-5, 1.87) * mm, "end": v(-5.02, 1.9) * mm});
            skLineSegment(sketch, "E319", {"start": v(-5.02, 1.9) * mm, "end": v(-5.04, 1.93) * mm});
            skLineSegment(sketch, "E320", {"start": v(-5.04, 1.93) * mm, "end": v(-5.06, 1.95) * mm});
            skLineSegment(sketch, "E321", {"start": v(-5.06, 1.95) * mm, "end": v(-5.1, 2) * mm});
            skLineSegment(sketch, "E322", {"start": v(-5.1, 2) * mm, "end": v(-5.15, 2.03) * mm});
            skLineSegment(sketch, "E323", {"start": v(-5.15, 2.03) * mm, "end": v(-5.2, 2.06) * mm});
            skLineSegment(sketch, "E324", {"start": v(-5.2, 2.06) * mm, "end": v(-5.3, 2.12) * mm});
            skLineSegment(sketch, "E325", {"start": v(-5.3, 2.12) * mm, "end": v(-5.4, 2.18) * mm});
            skLineSegment(sketch, "E326", {"start": v(-5.4, 2.18) * mm, "end": v(-5.5, 2.26) * mm});
            skLineSegment(sketch, "E327", {"start": v(-5.5, 2.26) * mm, "end": v(-5.6, 2.35) * mm});
            skLineSegment(sketch, "E328", {"start": v(-5.6, 2.35) * mm, "end": v(-5.68, 2.44) * mm});
            skLineSegment(sketch, "E329", {"start": v(-5.68, 2.44) * mm, "end": v(-5.77, 2.53) * mm});
            skLineSegment(sketch, "E330", {"start": v(-5.77, 2.53) * mm, "end": v(-5.85, 2.64) * mm});
            skLineSegment(sketch, "E331", {"start": v(-5.85, 2.64) * mm, "end": v(-5.93, 2.75) * mm});
            skLineSegment(sketch, "E332", {"start": v(-5.93, 2.75) * mm, "end": v(-6, 2.86) * mm});
            skLineSegment(sketch, "E333", {"start": v(-6, 2.86) * mm, "end": v(-6.08, 2.98) * mm});
            skLineSegment(sketch, "E334", {"start": v(-6.08, 2.98) * mm, "end": v(-6.15, 3.1) * mm});
            skLineSegment(sketch, "E335", {"start": v(-6.15, 3.1) * mm, "end": v(-6.21, 3.23) * mm});
            skLineSegment(sketch, "E336", {"start": v(-6.21, 3.23) * mm, "end": v(-5.9, 3.76) * mm});
            skLineSegment(sketch, "E337", {"start": v(-5.9, 3.76) * mm, "end": v(-5.76, 3.77) * mm});
            skLineSegment(sketch, "E338", {"start": v(-5.76, 3.77) * mm, "end": v(-5.62, 3.77) * mm});
            skLineSegment(sketch, "E339", {"start": v(-5.62, 3.77) * mm, "end": v(-5.48, 3.77) * mm});
            skLineSegment(sketch, "E340", {"start": v(-5.48, 3.77) * mm, "end": v(-5.34, 3.76) * mm});
            skLineSegment(sketch, "E341", {"start": v(-5.34, 3.76) * mm, "end": v(-5.21, 3.75) * mm});
            skLineSegment(sketch, "E342", {"start": v(-5.21, 3.75) * mm, "end": v(-5.08, 3.73) * mm});
            skLineSegment(sketch, "E343", {"start": v(-5.08, 3.73) * mm, "end": v(-4.95, 3.7) * mm});
            skLineSegment(sketch, "E344", {"start": v(-4.95, 3.7) * mm, "end": v(-4.83, 3.67) * mm});
            skLineSegment(sketch, "E345", {"start": v(-4.83, 3.67) * mm, "end": v(-4.7, 3.64) * mm});
            skLineSegment(sketch, "E346", {"start": v(-4.7, 3.64) * mm, "end": v(-4.6, 3.6) * mm});
            skLineSegment(sketch, "E347", {"start": v(-4.6, 3.6) * mm, "end": v(-4.49, 3.54) * mm});
            skLineSegment(sketch, "E348", {"start": v(-4.49, 3.54) * mm, "end": v(-4.39, 3.48) * mm});
            skLineSegment(sketch, "E349", {"start": v(-4.39, 3.48) * mm, "end": v(-4.33, 3.45) * mm});
            skLineSegment(sketch, "E350", {"start": v(-4.33, 3.45) * mm, "end": v(-4.28, 3.43) * mm});
            skLineSegment(sketch, "E351", {"start": v(-4.28, 3.43) * mm, "end": v(-4.22, 3.4) * mm});
            skLineSegment(sketch, "E352", {"start": v(-4.22, 3.4) * mm, "end": v(-4.19, 3.4) * mm});
            skLineSegment(sketch, "E353", {"start": v(-4.19, 3.4) * mm, "end": v(-4.15, 3.4) * mm});
            skLineSegment(sketch, "E354", {"start": v(-4.15, 3.4) * mm, "end": v(-4.12, 3.4) * mm});
            skLineSegment(sketch, "E355", {"start": v(-4.12, 3.4) * mm, "end": v(-4.08, 3.4) * mm});
            skLineSegment(sketch, "E356", {"start": v(-4.08, 3.4) * mm, "end": v(-4.03, 3.4) * mm});
            skLineSegment(sketch, "E357", {"start": v(-4.03, 3.4) * mm, "end": v(-3.94, 3.46) * mm});
            skLineSegment(sketch, "E358", {"start": v(-3.94, 3.46) * mm, "end": v(-3.7, 3.7) * mm});
            skLineSegment(sketch, "E359", {"start": v(-3.7, 3.7) * mm, "end": v(-3.46, 3.94) * mm});
            skLineSegment(sketch, "E360", {"start": v(-3.46, 3.94) * mm, "end": v(-3.4, 4.03) * mm});
            skLineSegment(sketch, "E361", {"start": v(-3.4, 4.03) * mm, "end": v(-3.4, 4.08) * mm});
            skLineSegment(sketch, "E362", {"start": v(-3.4, 4.08) * mm, "end": v(-3.4, 4.12) * mm});
            skLineSegment(sketch, "E363", {"start": v(-3.4, 4.12) * mm, "end": v(-3.4, 4.15) * mm});
            skLineSegment(sketch, "E364", {"start": v(-3.4, 4.15) * mm, "end": v(-3.4, 4.19) * mm});
            skLineSegment(sketch, "E365", {"start": v(-3.4, 4.19) * mm, "end": v(-3.4, 4.22) * mm});
            skLineSegment(sketch, "E366", {"start": v(-3.4, 4.22) * mm, "end": v(-3.43, 4.28) * mm});
            skLineSegment(sketch, "E367", {"start": v(-3.43, 4.28) * mm, "end": v(-3.45, 4.33) * mm});
            skLineSegment(sketch, "E368", {"start": v(-3.45, 4.33) * mm, "end": v(-3.48, 4.39) * mm});
            skLineSegment(sketch, "E369", {"start": v(-3.48, 4.39) * mm, "end": v(-3.54, 4.49) * mm});
            skLineSegment(sketch, "E370", {"start": v(-3.54, 4.49) * mm, "end": v(-3.6, 4.6) * mm});
            skLineSegment(sketch, "E371", {"start": v(-3.6, 4.6) * mm, "end": v(-3.64, 4.7) * mm});
            skLineSegment(sketch, "E372", {"start": v(-3.64, 4.7) * mm, "end": v(-3.67, 4.83) * mm});
            skLineSegment(sketch, "E373", {"start": v(-3.67, 4.83) * mm, "end": v(-3.7, 4.95) * mm});
            skLineSegment(sketch, "E374", {"start": v(-3.7, 4.95) * mm, "end": v(-3.73, 5.08) * mm});
            skLineSegment(sketch, "E375", {"start": v(-3.73, 5.08) * mm, "end": v(-3.75, 5.21) * mm});
            skLineSegment(sketch, "E376", {"start": v(-3.75, 5.21) * mm, "end": v(-3.76, 5.34) * mm});
            skLineSegment(sketch, "E377", {"start": v(-3.76, 5.34) * mm, "end": v(-3.77, 5.48) * mm});
            skLineSegment(sketch, "E378", {"start": v(-3.77, 5.48) * mm, "end": v(-3.77, 5.62) * mm});
            skLineSegment(sketch, "E379", {"start": v(-3.77, 5.62) * mm, "end": v(-3.77, 5.76) * mm});
            skLineSegment(sketch, "E380", {"start": v(-3.77, 5.76) * mm, "end": v(-3.76, 5.9) * mm});
            skLineSegment(sketch, "E381", {"start": v(-3.76, 5.9) * mm, "end": v(-3.23, 6.21) * mm});
            skLineSegment(sketch, "E382", {"start": v(-3.23, 6.21) * mm, "end": v(-3.1, 6.15) * mm});
            skLineSegment(sketch, "E383", {"start": v(-3.1, 6.15) * mm, "end": v(-2.98, 6.08) * mm});
            skLineSegment(sketch, "E384", {"start": v(-2.98, 6.08) * mm, "end": v(-2.86, 6) * mm});
            skLineSegment(sketch, "E385", {"start": v(-2.86, 6) * mm, "end": v(-2.75, 5.93) * mm});
            skLineSegment(sketch, "E386", {"start": v(-2.75, 5.93) * mm, "end": v(-2.64, 5.85) * mm});
            skLineSegment(sketch, "E387", {"start": v(-2.64, 5.85) * mm, "end": v(-2.53, 5.77) * mm});
            skLineSegment(sketch, "E388", {"start": v(-2.53, 5.77) * mm, "end": v(-2.44, 5.68) * mm});
            skLineSegment(sketch, "E389", {"start": v(-2.44, 5.68) * mm, "end": v(-2.35, 5.6) * mm});
            skLineSegment(sketch, "E390", {"start": v(-2.35, 5.6) * mm, "end": v(-2.26, 5.5) * mm});
            skLineSegment(sketch, "E391", {"start": v(-2.26, 5.5) * mm, "end": v(-2.18, 5.4) * mm});
            skLineSegment(sketch, "E392", {"start": v(-2.18, 5.4) * mm, "end": v(-2.12, 5.3) * mm});
            skLineSegment(sketch, "E393", {"start": v(-2.12, 5.3) * mm, "end": v(-2.06, 5.2) * mm});
            skLineSegment(sketch, "E394", {"start": v(-2.06, 5.2) * mm, "end": v(-2.03, 5.15) * mm});
            skLineSegment(sketch, "E395", {"start": v(-2.03, 5.15) * mm, "end": v(-2, 5.1) * mm});
            skLineSegment(sketch, "E396", {"start": v(-2, 5.1) * mm, "end": v(-1.95, 5.06) * mm});
            skLineSegment(sketch, "E397", {"start": v(-1.95, 5.06) * mm, "end": v(-1.93, 5.04) * mm});
            skLineSegment(sketch, "E398", {"start": v(-1.93, 5.04) * mm, "end": v(-1.9, 5.02) * mm});
            skLineSegment(sketch, "E399", {"start": v(-1.9, 5.02) * mm, "end": v(-1.87, 5) * mm});
            skLineSegment(sketch, "E400", {"start": v(-1.87, 5) * mm, "end": v(-1.83, 4.98) * mm});
            skLineSegment(sketch, "E401", {"start": v(-1.83, 4.98) * mm, "end": v(-1.79, 4.96) * mm});
            skLineSegment(sketch, "E402", {"start": v(-1.79, 4.96) * mm, "end": v(-1.69, 4.97) * mm});
            skLineSegment(sketch, "E403", {"start": v(-1.69, 4.97) * mm, "end": v(-1.36, 5.07) * mm});
            skLineSegment(sketch, "E404", {"start": v(-1.36, 5.07) * mm, "end": v(-1.02, 5.15) * mm});
            skLineSegment(sketch, "E405", {"start": v(-1.02, 5.15) * mm, "end": v(-0.93, 5.2) * mm});
            skLineSegment(sketch, "E406", {"start": v(-0.93, 5.2) * mm, "end": v(-0.9, 5.23) * mm});
            skLineSegment(sketch, "E407", {"start": v(-0.9, 5.23) * mm, "end": v(-0.88, 5.26) * mm});
            skLineSegment(sketch, "E408", {"start": v(-0.88, 5.26) * mm, "end": v(-0.86, 5.3) * mm});
            skLineSegment(sketch, "E409", {"start": v(-0.86, 5.3) * mm, "end": v(-0.85, 5.33) * mm});
            skLineSegment(sketch, "E410", {"start": v(-0.85, 5.33) * mm, "end": v(-0.84, 5.36) * mm});
            skLineSegment(sketch, "E411", {"start": v(-0.84, 5.36) * mm, "end": v(-0.83, 5.42) * mm});
            skLineSegment(sketch, "E412", {"start": v(-0.83, 5.42) * mm, "end": v(-0.82, 5.48) * mm});
            skLineSegment(sketch, "E413", {"start": v(-0.82, 5.48) * mm, "end": v(-0.82, 5.54) * mm});
            skLineSegment(sketch, "E414", {"start": v(-0.82, 5.54) * mm, "end": v(-0.82, 5.66) * mm});
            skLineSegment(sketch, "E415", {"start": v(-0.82, 5.66) * mm, "end": v(-0.81, 5.78) * mm});
            skLineSegment(sketch, "E416", {"start": v(-0.81, 5.78) * mm, "end": v(-0.8, 5.9) * mm});
            skLineSegment(sketch, "E417", {"start": v(-0.8, 5.9) * mm, "end": v(-0.77, 6.02) * mm});
            skLineSegment(sketch, "E418", {"start": v(-0.77, 6.02) * mm, "end": v(-0.73, 6.14) * mm});
            skLineSegment(sketch, "E419", {"start": v(-0.73, 6.14) * mm, "end": v(-0.69, 6.26) * mm});
            skLineSegment(sketch, "E420", {"start": v(-0.69, 6.26) * mm, "end": v(-0.64, 6.39) * mm});
            skLineSegment(sketch, "E421", {"start": v(-0.64, 6.39) * mm, "end": v(-0.59, 6.5) * mm});
            skLineSegment(sketch, "E422", {"start": v(-0.59, 6.5) * mm, "end": v(-0.52, 6.63) * mm});
            skLineSegment(sketch, "E423", {"start": v(-0.52, 6.63) * mm, "end": v(-0.46, 6.75) * mm});
            skLineSegment(sketch, "E424", {"start": v(-0.46, 6.75) * mm, "end": v(-0.39, 6.88) * mm});
            skLineSegment(sketch, "E425", {"start": v(-0.39, 6.88) * mm, "end": v(-0.3, 7) * mm});
            skLineSegment(sketch, "E426", {"start": v(-0.3, 7) * mm, "end": v(0.3, 7) * mm});
            skLineSegment(sketch, "E427", {"start": v(0.3, 7) * mm, "end": v(0.39, 6.88) * mm});
            skLineSegment(sketch, "E428", {"start": v(0.39, 6.88) * mm, "end": v(0.46, 6.75) * mm});
            skLineSegment(sketch, "E429", {"start": v(0.46, 6.75) * mm, "end": v(0.52, 6.63) * mm});
            skLineSegment(sketch, "E430", {"start": v(0.52, 6.63) * mm, "end": v(0.59, 6.5) * mm});
            skLineSegment(sketch, "E431", {"start": v(0.59, 6.5) * mm, "end": v(0.64, 6.39) * mm});
            skLineSegment(sketch, "E432", {"start": v(0.64, 6.39) * mm, "end": v(0.69, 6.26) * mm});
            skLineSegment(sketch, "E433", {"start": v(0.69, 6.26) * mm, "end": v(0.73, 6.14) * mm});
            skLineSegment(sketch, "E434", {"start": v(0.73, 6.14) * mm, "end": v(0.77, 6.02) * mm});
            skLineSegment(sketch, "E435", {"start": v(0.77, 6.02) * mm, "end": v(0.8, 5.9) * mm});
            skLineSegment(sketch, "E436", {"start": v(0.8, 5.9) * mm, "end": v(0.81, 5.78) * mm});
            skLineSegment(sketch, "E437", {"start": v(0.81, 5.78) * mm, "end": v(0.82, 5.66) * mm});
            skLineSegment(sketch, "E438", {"start": v(0.82, 5.66) * mm, "end": v(0.82, 5.54) * mm});
            skLineSegment(sketch, "E439", {"start": v(0.82, 5.54) * mm, "end": v(0.82, 5.48) * mm});
            skLineSegment(sketch, "E440", {"start": v(0.82, 5.48) * mm, "end": v(0.83, 5.42) * mm});
            skLineSegment(sketch, "E441", {"start": v(0.83, 5.42) * mm, "end": v(0.84, 5.36) * mm});
            skLineSegment(sketch, "E442", {"start": v(0.84, 5.36) * mm, "end": v(0.85, 5.33) * mm});
            skLineSegment(sketch, "E443", {"start": v(0.85, 5.33) * mm, "end": v(0.86, 5.3) * mm});
            skLineSegment(sketch, "E444", {"start": v(0.86, 5.3) * mm, "end": v(0.88, 5.26) * mm});
            skLineSegment(sketch, "E445", {"start": v(0.88, 5.26) * mm, "end": v(0.9, 5.23) * mm});
            skLineSegment(sketch, "E446", {"start": v(0.9, 5.23) * mm, "end": v(0.93, 5.2) * mm});
            skLineSegment(sketch, "E447", {"start": v(0.93, 5.2) * mm, "end": v(1.02, 5.15) * mm});
            skLineSegment(sketch, "E448", {"start": v(1.02, 5.15) * mm, "end": v(1.36, 5.07) * mm});
            skLineSegment(sketch, "E449", {"start": v(1.36, 5.07) * mm, "end": v(1.69, 4.97) * mm});
            skLineSegment(sketch, "E450", {"start": v(1.69, 4.97) * mm, "end": v(1.79, 4.96) * mm});
            skLineSegment(sketch, "E451", {"start": v(1.79, 4.96) * mm, "end": v(1.83, 4.98) * mm});
            skLineSegment(sketch, "E452", {"start": v(1.83, 4.98) * mm, "end": v(1.87, 5) * mm});
            skLineSegment(sketch, "E453", {"start": v(1.87, 5) * mm, "end": v(1.9, 5.02) * mm});
            skLineSegment(sketch, "E454", {"start": v(1.9, 5.02) * mm, "end": v(1.93, 5.04) * mm});
            skLineSegment(sketch, "E455", {"start": v(1.93, 5.04) * mm, "end": v(1.95, 5.06) * mm});
            skLineSegment(sketch, "E456", {"start": v(1.95, 5.06) * mm, "end": v(2, 5.1) * mm});
            skLineSegment(sketch, "E457", {"start": v(2, 5.1) * mm, "end": v(2.03, 5.15) * mm});
            skLineSegment(sketch, "E458", {"start": v(2.03, 5.15) * mm, "end": v(2.06, 5.2) * mm});
            skLineSegment(sketch, "E459", {"start": v(2.06, 5.2) * mm, "end": v(2.12, 5.3) * mm});
            skLineSegment(sketch, "E460", {"start": v(2.12, 5.3) * mm, "end": v(2.18, 5.4) * mm});
            skLineSegment(sketch, "E461", {"start": v(2.18, 5.4) * mm, "end": v(2.26, 5.5) * mm});
            skLineSegment(sketch, "E462", {"start": v(2.26, 5.5) * mm, "end": v(2.35, 5.6) * mm});
            skLineSegment(sketch, "E463", {"start": v(2.35, 5.6) * mm, "end": v(2.44, 5.68) * mm});
            skLineSegment(sketch, "E464", {"start": v(2.44, 5.68) * mm, "end": v(2.53, 5.77) * mm});
            skLineSegment(sketch, "E465", {"start": v(2.53, 5.77) * mm, "end": v(2.64, 5.85) * mm});
            skLineSegment(sketch, "E466", {"start": v(2.64, 5.85) * mm, "end": v(2.75, 5.93) * mm});
            skLineSegment(sketch, "E467", {"start": v(2.75, 5.93) * mm, "end": v(2.86, 6) * mm});
            skLineSegment(sketch, "E468", {"start": v(2.86, 6) * mm, "end": v(2.98, 6.08) * mm});
            skLineSegment(sketch, "E469", {"start": v(2.98, 6.08) * mm, "end": v(3.1, 6.15) * mm});
            skLineSegment(sketch, "E470", {"start": v(3.1, 6.15) * mm, "end": v(3.23, 6.21) * mm});
            skLineSegment(sketch, "E471", {"start": v(3.23, 6.21) * mm, "end": v(3.76, 5.9) * mm});
            skLineSegment(sketch, "E472", {"start": v(3.76, 5.9) * mm, "end": v(3.77, 5.76) * mm});
            skLineSegment(sketch, "E473", {"start": v(3.77, 5.76) * mm, "end": v(3.77, 5.62) * mm});
            skLineSegment(sketch, "E474", {"start": v(3.77, 5.62) * mm, "end": v(3.77, 5.48) * mm});
            skLineSegment(sketch, "E475", {"start": v(3.77, 5.48) * mm, "end": v(3.76, 5.34) * mm});
            skLineSegment(sketch, "E476", {"start": v(3.76, 5.34) * mm, "end": v(3.75, 5.21) * mm});
            skLineSegment(sketch, "E477", {"start": v(3.75, 5.21) * mm, "end": v(3.73, 5.08) * mm});
            skLineSegment(sketch, "E478", {"start": v(3.73, 5.08) * mm, "end": v(3.7, 4.95) * mm});
            skLineSegment(sketch, "E479", {"start": v(3.7, 4.95) * mm, "end": v(3.67, 4.83) * mm});
            skLineSegment(sketch, "E480", {"start": v(3.67, 4.83) * mm, "end": v(3.64, 4.7) * mm});
            skLineSegment(sketch, "E481", {"start": v(3.64, 4.7) * mm, "end": v(3.6, 4.6) * mm});
            skLineSegment(sketch, "E482", {"start": v(3.6, 4.6) * mm, "end": v(3.54, 4.49) * mm});
            skLineSegment(sketch, "E483", {"start": v(3.54, 4.49) * mm, "end": v(3.48, 4.39) * mm});
            skLineSegment(sketch, "E484", {"start": v(3.48, 4.39) * mm, "end": v(3.45, 4.33) * mm});
            skLineSegment(sketch, "E485", {"start": v(3.45, 4.33) * mm, "end": v(3.43, 4.28) * mm});
            skLineSegment(sketch, "E486", {"start": v(3.43, 4.28) * mm, "end": v(3.4, 4.22) * mm});
            skLineSegment(sketch, "E487", {"start": v(3.4, 4.22) * mm, "end": v(3.4, 4.19) * mm});
            skLineSegment(sketch, "E488", {"start": v(3.4, 4.19) * mm, "end": v(3.4, 4.15) * mm});
            skLineSegment(sketch, "E489", {"start": v(3.4, 4.15) * mm, "end": v(3.4, 4.12) * mm});
            skLineSegment(sketch, "E490", {"start": v(3.4, 4.12) * mm, "end": v(3.4, 4.08) * mm});
            skLineSegment(sketch, "E491", {"start": v(3.4, 4.08) * mm, "end": v(3.4, 4.03) * mm});
            skLineSegment(sketch, "E492", {"start": v(3.4, 4.03) * mm, "end": v(3.46, 3.94) * mm});
            skLineSegment(sketch, "E493", {"start": v(3.46, 3.94) * mm, "end": v(3.7, 3.7) * mm});
            skLineSegment(sketch, "E494", {"start": v(3.7, 3.7) * mm, "end": v(3.94, 3.46) * mm});
            skLineSegment(sketch, "E495", {"start": v(3.94, 3.46) * mm, "end": v(4.03, 3.4) * mm});
            skLineSegment(sketch, "E496", {"start": v(4.03, 3.4) * mm, "end": v(4.08, 3.4) * mm});
            skLineSegment(sketch, "E497", {"start": v(4.08, 3.4) * mm, "end": v(4.12, 3.4) * mm});
            skLineSegment(sketch, "E498", {"start": v(4.12, 3.4) * mm, "end": v(4.15, 3.4) * mm});
            skLineSegment(sketch, "E499", {"start": v(4.15, 3.4) * mm, "end": v(4.19, 3.4) * mm});
            skLineSegment(sketch, "E500", {"start": v(4.19, 3.4) * mm, "end": v(4.22, 3.4) * mm});
            skLineSegment(sketch, "E501", {"start": v(4.22, 3.4) * mm, "end": v(4.28, 3.43) * mm});
            skLineSegment(sketch, "E502", {"start": v(4.28, 3.43) * mm, "end": v(4.33, 3.45) * mm});
            skLineSegment(sketch, "E503", {"start": v(4.33, 3.45) * mm, "end": v(4.39, 3.48) * mm});
            skLineSegment(sketch, "E504", {"start": v(4.39, 3.48) * mm, "end": v(4.49, 3.54) * mm});
            skLineSegment(sketch, "E505", {"start": v(4.49, 3.54) * mm, "end": v(4.6, 3.6) * mm});
            skLineSegment(sketch, "E506", {"start": v(4.6, 3.6) * mm, "end": v(4.7, 3.64) * mm});
            skLineSegment(sketch, "E507", {"start": v(4.7, 3.64) * mm, "end": v(4.83, 3.67) * mm});
            skLineSegment(sketch, "E508", {"start": v(4.83, 3.67) * mm, "end": v(4.95, 3.7) * mm});
            skLineSegment(sketch, "E509", {"start": v(4.95, 3.7) * mm, "end": v(5.08, 3.73) * mm});
            skLineSegment(sketch, "E510", {"start": v(5.08, 3.73) * mm, "end": v(5.21, 3.75) * mm});
            skLineSegment(sketch, "E511", {"start": v(5.21, 3.75) * mm, "end": v(5.34, 3.76) * mm});
            skLineSegment(sketch, "E512", {"start": v(5.34, 3.76) * mm, "end": v(5.48, 3.77) * mm});
            skLineSegment(sketch, "E513", {"start": v(5.48, 3.77) * mm, "end": v(5.62, 3.77) * mm});
            skLineSegment(sketch, "E514", {"start": v(5.62, 3.77) * mm, "end": v(5.76, 3.77) * mm});
            skLineSegment(sketch, "E515", {"start": v(5.76, 3.77) * mm, "end": v(5.9, 3.76) * mm});
            skLineSegment(sketch, "E516", {"start": v(5.9, 3.76) * mm, "end": v(6.21, 3.23) * mm});
            skLineSegment(sketch, "E517", {"start": v(6.21, 3.23) * mm, "end": v(6.15, 3.1) * mm});
            skLineSegment(sketch, "E518", {"start": v(6.15, 3.1) * mm, "end": v(6.08, 2.98) * mm});
            skLineSegment(sketch, "E519", {"start": v(6.08, 2.98) * mm, "end": v(6, 2.86) * mm});
            skLineSegment(sketch, "E520", {"start": v(6, 2.86) * mm, "end": v(5.93, 2.75) * mm});
            skLineSegment(sketch, "E521", {"start": v(5.93, 2.75) * mm, "end": v(5.85, 2.64) * mm});
            skLineSegment(sketch, "E522", {"start": v(5.85, 2.64) * mm, "end": v(5.77, 2.53) * mm});
            skLineSegment(sketch, "E523", {"start": v(5.77, 2.53) * mm, "end": v(5.68, 2.44) * mm});
            skLineSegment(sketch, "E524", {"start": v(5.68, 2.44) * mm, "end": v(5.6, 2.35) * mm});
            skLineSegment(sketch, "E525", {"start": v(5.6, 2.35) * mm, "end": v(5.5, 2.26) * mm});
            skLineSegment(sketch, "E526", {"start": v(5.5, 2.26) * mm, "end": v(5.4, 2.18) * mm});
            skLineSegment(sketch, "E527", {"start": v(5.4, 2.18) * mm, "end": v(5.3, 2.12) * mm});
            skLineSegment(sketch, "E528", {"start": v(5.3, 2.12) * mm, "end": v(5.2, 2.06) * mm});
            skLineSegment(sketch, "E529", {"start": v(5.2, 2.06) * mm, "end": v(5.15, 2.03) * mm});
            skLineSegment(sketch, "E530", {"start": v(5.15, 2.03) * mm, "end": v(5.1, 2) * mm});
            skLineSegment(sketch, "E531", {"start": v(5.1, 2) * mm, "end": v(5.06, 1.95) * mm});
            skLineSegment(sketch, "E532", {"start": v(5.06, 1.95) * mm, "end": v(5.04, 1.93) * mm});
            skLineSegment(sketch, "E533", {"start": v(5.04, 1.93) * mm, "end": v(5.02, 1.9) * mm});
            skLineSegment(sketch, "E534", {"start": v(5.02, 1.9) * mm, "end": v(5, 1.87) * mm});
            skLineSegment(sketch, "E535", {"start": v(5, 1.87) * mm, "end": v(4.98, 1.83) * mm});
            skLineSegment(sketch, "E536", {"start": v(4.98, 1.83) * mm, "end": v(4.96, 1.79) * mm});
            skLineSegment(sketch, "E537", {"start": v(4.96, 1.79) * mm, "end": v(4.97, 1.69) * mm});
            skLineSegment(sketch, "E538", {"start": v(4.97, 1.69) * mm, "end": v(5.07, 1.36) * mm});
            skLineSegment(sketch, "E539", {"start": v(5.07, 1.36) * mm, "end": v(5.15, 1.02) * mm});
            skLineSegment(sketch, "E540", {"start": v(-2.33, 0) * mm, "end": v(2.33, 0) * mm, "construction": true});
            skLineSegment(sketch, "E541", {"start": v(0, -2.33) * mm, "end": v(0, 2.33) * mm, "construction": true});
            skCircle(sketch, "E542", {"center": v(0, 0) * mm, "radius": 3 * mm});
            skSolve(sketch);
        }
        {
            var Q0;
            Q0=makeQuery(id+"F0.imprint","IMPRINT",FACE,{"disambiguationData":[TD([[makeQuery(id+"F0.imprint","IMPRINT",EDGE,{"derivedFrom":sQuery(id+"F0.wireOp",EDGE,"E0")}),-1.0]])]});
            extrude(context, id + "F1", {"entities" : qUnion([Q0]), "depth" : 5 * mm});
        }
    });
